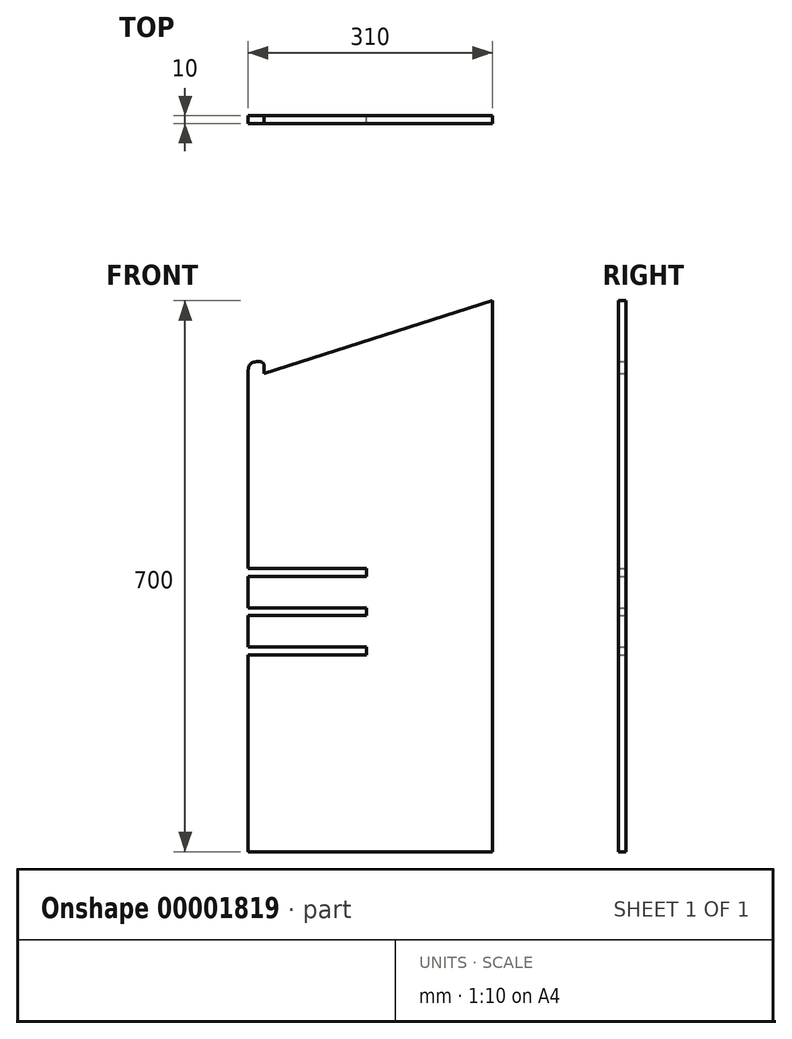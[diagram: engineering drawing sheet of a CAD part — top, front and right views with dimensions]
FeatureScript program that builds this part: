
annotation { "Feature Type Name" : "Feature", "Feature Type Description" : "" }
export const myFeature = defineFeature(function(context is Context, id is Id, definition is map)
    precondition{}
    {
        {
            var Q0;
            Q0=qCreatedBy(makeId("Front.planeOp"),FACE);
            var sketch = newSketch(context, id + "F0", { "sketchPlane" : qUnion([Q0])});
            skLineSegment(sketch, "E0.bottom", {"start": v(0, 0) * mm, "end": v(310, 0) * mm});
            skLineSegment(sketch, "E0.left", {"start": v(0, 0) * mm, "end": v(0, 250) * mm});
            skLineSegment(sketch, "E0.right", {"start": v(310, 0) * mm, "end": v(310, 700) * mm});
            skLineSegment(sketch, "E1", {"start": v(20, 617.49) * mm, "end": v(20, 607.49) * mm});
            skLineSegment(sketch, "E2", {"start": v(20, 607.49) * mm, "end": v(0, 607.49) * mm});
            skLineSegment(sketch, "E3", {"start": v(20, 607.49) * mm, "end": v(310, 700) * mm});
            skLineSegment(sketch, "E4", {"start": v(15, 622.49) * mm, "end": v(10, 622.49) * mm});
            skLineSegment(sketch, "E5", {"start": v(0, 300) * mm, "end": v(150, 300) * mm});
            skLineSegment(sketch, "E6", {"start": v(150, 300) * mm, "end": v(150, 310) * mm});
            skLineSegment(sketch, "E7", {"start": v(150, 310) * mm, "end": v(0, 310) * mm});
            skLineSegment(sketch, "E8.trimOffspring", {"start": v(0, 310) * mm, "end": v(0, 350) * mm});
            skLineSegment(sketch, "E9.bottom", {"start": v(0, 360) * mm, "end": v(150, 360) * mm});
            skLineSegment(sketch, "E9.top", {"start": v(0, 350) * mm, "end": v(150, 350) * mm});
            skLineSegment(sketch, "E9.right", {"start": v(150, 360) * mm, "end": v(150, 350) * mm});
            skLineSegment(sketch, "E10.bottom", {"start": v(0, 260) * mm, "end": v(150, 260) * mm});
            skLineSegment(sketch, "E10.top", {"start": v(0, 250) * mm, "end": v(150, 250) * mm});
            skLineSegment(sketch, "E10.right", {"start": v(150, 260) * mm, "end": v(150, 250) * mm});
            skLineSegment(sketch, "E11.trimOffspring", {"start": v(0, 260) * mm, "end": v(0, 300) * mm});
            skLineSegment(sketch, "E12.trimOffspring", {"start": v(0, 360) * mm, "end": v(0, 612.49) * mm});
            skPoint(sketch, "E13.visualSharp", {"position": v(0, 622.49) * mm});
            skArc(sketch, "E13.filletArc", {"start": v(10, 622.49) * mm, "mid": v(2.93, 619.56) * mm, "end": v(0, 612.49) * mm});
            skPoint(sketch, "E14.visualSharp", {"position": v(20, 622.49) * mm});
            skArc(sketch, "E14.filletArc", {"start": v(20, 617.49) * mm, "mid": v(18.54, 621.02) * mm, "end": v(15, 622.49) * mm});
            skSolve(sketch);
        }
        {
            var Q0;
            Q0 = qSketchRegion(id + "F0", true);
            extrude(context, id + "F1", {"entities" : qUnion([Q0]), "depth" : 10 * mm});
        }
    });
